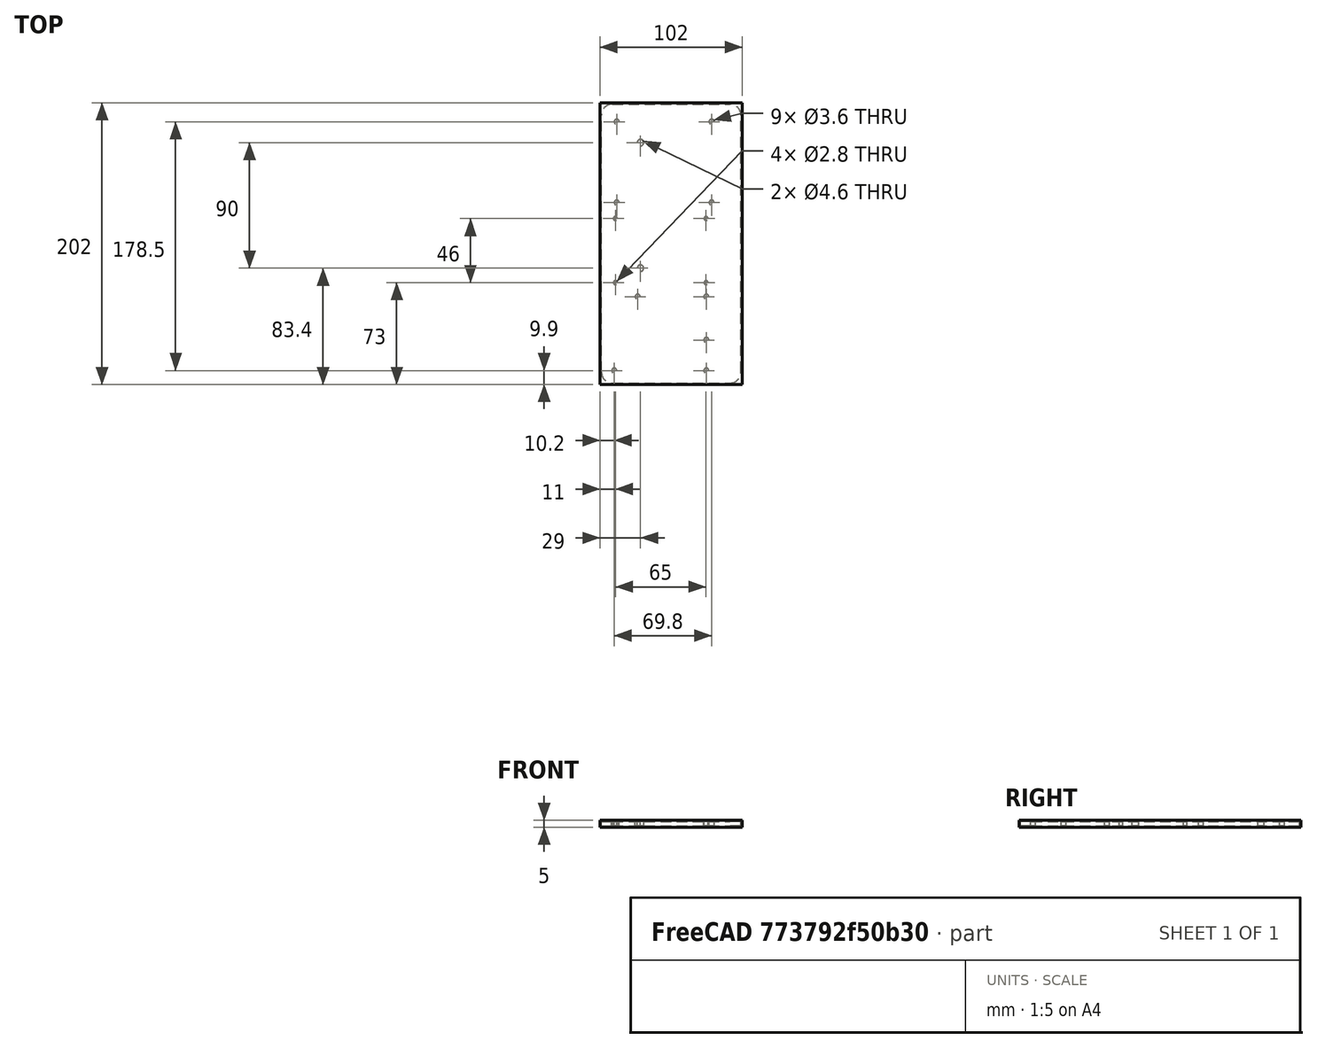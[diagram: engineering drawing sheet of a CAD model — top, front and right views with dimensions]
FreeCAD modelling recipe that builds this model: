
FCSTD DOCUMENT  (FreeCAD 0.18.4R)
Label: cnc_encoders_jobs
License: All rights reserved
LicenseURL: http://en.wikipedia.org/wiki/All_rights_reserved
objects: Path::FeaturePython×4, Part::FeaturePython×2, Part::Feature×1, App::FeaturePython×1, App::DocumentObjectGroup×1, Path::FeatureCompoundPython×1
note: 4 computed .brp shape members not serialized (recipe doc carries the construction recipe); baked Part::Feature solids carry a one-line shape summary decoded from their .brp

FEATURE [Part::Feature] Cut008_solid  label="cnc v4 plate cut (Solid)"
  shape: bbox 100 x 200 x 3 mm, 25 faces (baked)
FEATURE [App::FeaturePython] SetupSheet  # Path/CAM operation (typed FeaturePython)
  ClearanceHeightExpression = OpStockZMax+SetupSheet.ClearanceHeightOffset
  ClearanceHeightOffset = 0
  FinalDepthExpression = OpFinalDepth
  HorizRapid = 100
  SafeHeightExpression = OpStockZMax+SetupSheet.SafeHeightOffset
  SafeHeightOffset = 0
  StartDepthExpression = OpStartDepth
  StepDownExpression = OpToolDiameter
  VertRapid = 100
FEATURE [Part::FeaturePython] Clone  label="Model-cnc v4 plate cut (Solid)"  # Draft clone (typed FeaturePython)
  AttacherType = Attacher::AttachEngine3D
  Fuse = false
  Objects = -> [Cut008_solid]
  PathResource = Model
  Scale = (1,1,1)
FEATURE [App::DocumentObjectGroup] Model
  Group = -> [Clone]
FEATURE [Path::FeaturePython] T3__laser  label="T3: laser"  # Path/CAM operation (typed FeaturePython)
  HorizFeed = 0.5
  HorizRapid = 100
  SpindleDir = 0
  SpindleSpeed = 1000
  ToolNumber = 3
  VertFeed = 0.5
  VertRapid = 100
  expr: VertRapid = SetupSheet.VertRapid
  expr: HorizRapid = SetupSheet.HorizRapid
FEATURE [Part::FeaturePython] Stock  # WARN: FeaturePython — macro-defined, semantics opaque (R4)
  Base = -> Model
  ExtXneg = 1
  ExtXpos = 1
  ExtYneg = 1
  ExtYpos = 1
  ExtZneg = 1
  ExtZpos = 1
  Placement = pos=(-1.8e-15,-1.8e-15,0) rot=(0,0,1;0rad)
  StockType = FromBase
FEATURE [Path::FeaturePython] Engrave  # Path/CAM operation (typed FeaturePython)
  Active = true
  Base = -> [Clone]
  ClearanceHeight = 0
  FinalDepth = 0
  OpFinalDepth = 2.8
  OpStartDepth = 3
  OpStockZMax = 4
  OpStockZMin = -1
  OpToolDiameter = 0.2
  SafeHeight = 0
  StartDepth = 0.1
  StartVertex = 0
  StepDown = 0.2
  ToolController = -> T3__laser
  expr: StepDown = OpToolDiameter
FEATURE [Path::FeaturePython] Contour  # Path/CAM operation (typed FeaturePython)
  Active = true
  AreaParams:
    Tolerance = 1e-07
    FitArcs = True
    Simplify = False
    CleanDistance = 0.0
    Accuracy = 0.01
    Unit = 1.0
    MinArcPoints = 4
    MaxArcPoints = 100
    ClipperScale = 10000000.0
    Fill = 0
    Coplanar = 2
    Reorient = True
    Outline = False
    Explode = False
    OpenMode = 0
    Deflection = 0.01
    SubjectFill = 0
    ClipFill = 0
    Offset = 0.1
    ExtraPass = 0
    Stepover = 0.0
    LastStepover = 0.0
    JoinType = 0
    EndType = 0
    MiterLimit = 2.0
    RoundPrecision = 0.0
    PocketMode = 0
    ToolRadius = 1.0
    PocketExtraOffset = 0.0
    PocketStepover = 0.0
    PocketLastStepover = 0.0
    FromCenter = False
    Angle = 45.0
    AngleShift = 0.0
    Shift = 0.0
    Thicken = False
    SectionCount = -1
    Stepdown = 1.0
    SectionOffset = 0.0
    SectionTolerance = 1e-06
    SectionMode = 2
    Project = False
  ClearanceHeight = 4
  Direction = 0
  FinalDepth = 0
  JoinType = 0
  MiterLimit = 0.1
  OffsetExtra = 0
  OpFinalDepth = -1
  OpStartDepth = 4
  OpStockZMax = 4
  OpStockZMin = -1
  OpToolDiameter = 0.2
  PathParams = {'orientation': 1, 'feedrate': 0.5, 'feedrate_v': 0.5, 'verbose': True, 'resume_height': 4.0, 'retraction': 4.0, 'return_end': True, 'preamble': False}
  SafeHeight = 4
  Side = 0
  StartDepth = 0.1
  StartPoint = (0,0,0)
  StepDown = 0.2
  ToolController = -> T3__laser
  UseComp = true
  UseStartPoint = false
  expr: ClearanceHeight = OpStockZMax + SetupSheet.ClearanceHeightOffset
  expr: SafeHeight = OpStockZMax + SetupSheet.SafeHeightOffset
  expr: StepDown = OpToolDiameter
FEATURE [Path::FeatureCompoundPython] Operations  # Path/CAM operation (typed FeaturePython)
  Group = -> [Engrave,Contour]
  UsePlacements = false
FEATURE [Path::FeaturePython] Job  label="cnc v4 plate cut (Solid) job"  # Path/CAM operation (typed FeaturePython)
  GeometryTolerance = 0.01
  Model = -> Model
  Operations = -> Operations
  PostProcessor = 1
  PostProcessorOutputFile = <userpath>/work/roborep/freecad/microscope/cnc_encoders_plate.gcode
  SetupSheet = -> SetupSheet
  Stock = -> Stock
  ToolController = -> [T3__laser]
